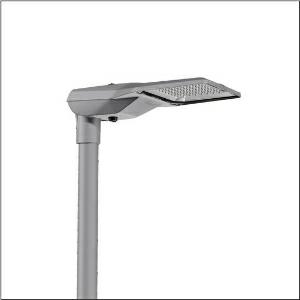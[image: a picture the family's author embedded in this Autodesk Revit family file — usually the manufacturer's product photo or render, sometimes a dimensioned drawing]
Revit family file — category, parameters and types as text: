
# Revit family: streetlight_sl_21_midi___st0_8a_5xe3c33t08nb_d41b
name_source: partatom
category: Lighting Fixtures
units: mm (PartAtom-declared; Revit-internal decimal feet)

## family parameters
Cut with Voids When Loaded = No
Host = Face
Light Source = No
Part Type = Normal
Room Calculation Point = No
Round Connector Dimension = Use Diameter
Shared = No

## types (1)
- --- (1 x LED, 22700 lm, 151.2 W, 3000K)
    Apparent Load = 151 VA
    CIE Flux Codes = 41 75 97 100 100
    Color Rendering = 70
    Color Temperature = 3000K
    Default Elevation = 1800 mm
    Description = Streetlight SL 21 midi, mast luminaire, primary light control with lens, of PMMA, primary optical cover: cover, of toughened safety glass, transparent, light distribution: ST0.8a, light emission: direct distribution, primary light characteristic: asymmetric, installation type: side-entry, post-top, LED, High Power LED, rated luminous flux: 22.700lm, luminous efficacy: 150lm/W, light colour: 730, colour temperature: 3000K, control gear: D4i, control: overheat protection, constant luminous flux control, time-dependent luminous flux control, flexible luminous flux parameterisation, pre-setting: logarithmic dimming characteristic, mains connection: 230..240V, AC, 50/60Hz, start of lifetime: 151W, end of service life: 157W, reduction: 70W, luminaire housing, of diecast aluminium, powder-coated, Siteco® metallic grey (DB 702S), corrosivity category C5 mid according to DIN EN ISO 12944, please order mast flange separately, inclination adjustable: 0°, 5°, 10°, 15°, sealing non-destructively replaceable, multi-level sealing system, length: 644mm, width: 335mm, height: 110mm, mast flange for spigot size: 42mm (side-entry): 5XC10008XM4, 60/48mm (side-entry/post-top): 5XC10108XM2, 76/60mm (side-entry/post-top): 5XC10108XM1, mounting height: 4..8m, Smart Interface below and above, protection rating (complete): IP66, insulation class (complete): insulation class II (safety insulation), certification: CE, ENEC, ENEC+, VDE, impact resistance: IK10, permissible operating ambient temperature for outdoor applications: -40..+50°C, standard-compliant lighting for roads and squares, packaging unit: 1 piece

Light Distribution: ST0.8a
    Height = 111 mm
    Lamp = 1 x LED
    Lamp Light Flux = 22700 lm
    Lamp Power = 151.2 W
    Lamp count = 1
    Length = 644 mm
    Luminous efficacy = 150 lm/W
    Manufacturer = Siteco
    ModVariant = No
    Model = 5XE3C33T08NB
    Number of Poles = 1
    OnlyDefault = Yes
    Power Factor = 1
    Product Name = Streetlight SL 21 midi | ST0.8a
    Product group = mast luminaire | pylon top
    ProductGroupID = 6100
    Protection Class = Protection class II
    Protection Degree = IP 66
    RLX_Detail_Level = 1
    RLX_Emergency_Light_Flux = 0 lm
    RLX_Emergency_Type = 0
    RLX_Emergency_Type_DB = No
    RlxData = <blob elided: 27053 chars, md5=d9f57c5b>
    Socket = socket
    Standby Power = 0 W
    System Light Flux = 22700 lm
    System Power = 151 W
    Type Comments = factory setting: luminous flux: 100 % | dim-lin: 254 | 802 mA
    Type Image = l_1004304.jpg
    URL = http://relux.com
    VarID = @adj_190109
    Voltage = 0 V
    Weight = 0.00 kg
    Width = 336 mm

## geometry (parser evidence)
native form markers: Blend x4, Sweep x12
no freeform markers — native parametric forms only
